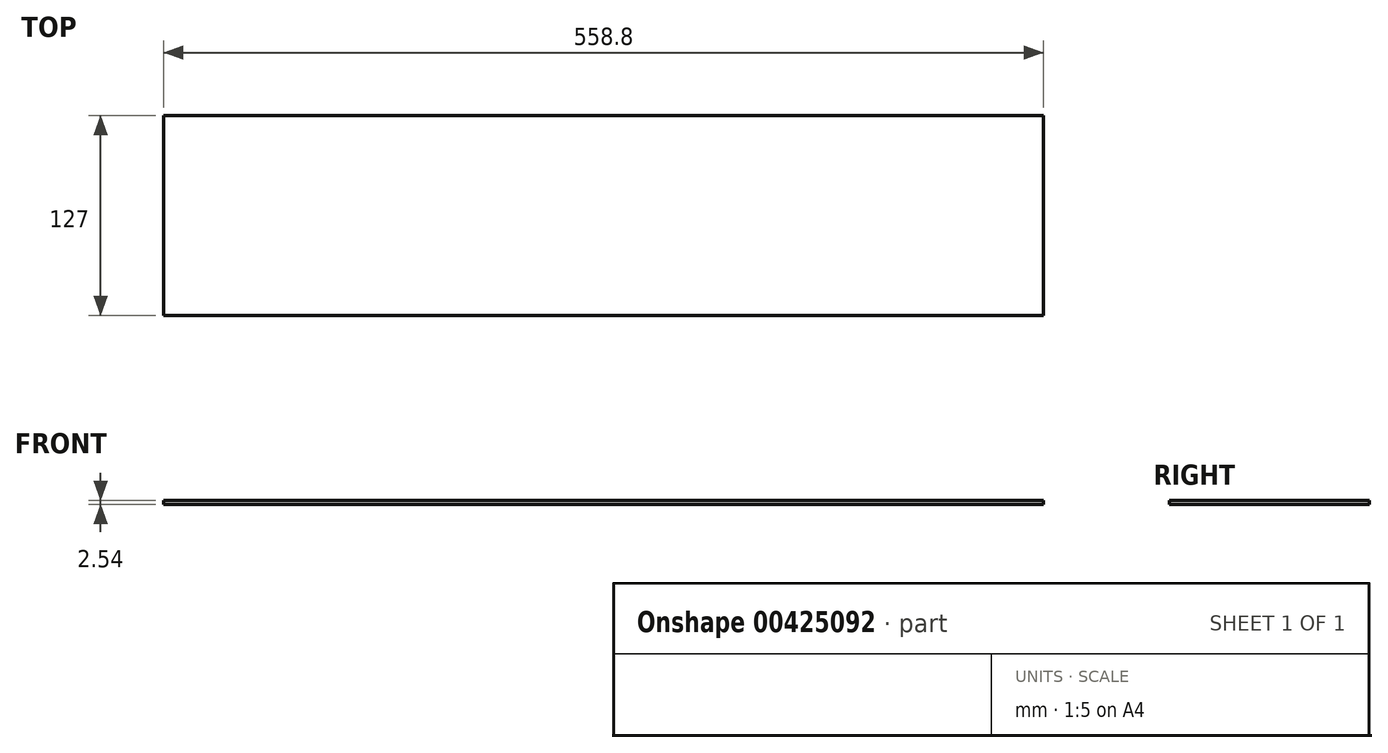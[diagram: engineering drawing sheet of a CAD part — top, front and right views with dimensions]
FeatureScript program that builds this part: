
annotation { "Feature Type Name" : "Feature", "Feature Type Description" : "" }
export const myFeature = defineFeature(function(context is Context, id is Id, definition is map)
    precondition{}
    {
        {
            var Q0;
            Q0=qCreatedBy(makeId("Front.planeOp"),FACE);
            var sketch = newSketch(context, id + "F0", { "sketchPlane" : qUnion([Q0])});
            skLineSegment(sketch, "E0.bottom", {"start": v(-871.4, 83) * mm, "end": v(-312.6, 83) * mm});
            skLineSegment(sketch, "E0.top", {"start": v(-871.4, 80.45) * mm, "end": v(-312.6, 80.45) * mm});
            skLineSegment(sketch, "E0.left", {"start": v(-871.4, 83) * mm, "end": v(-871.4, 80.45) * mm});
            skLineSegment(sketch, "E0.right", {"start": v(-312.6, 83) * mm, "end": v(-312.6, 80.45) * mm});
            skSolve(sketch);
        }
        {
            var Q0;
            Q0=makeQuery(id+"F0.imprint","IMPRINT",FACE,{"disambiguationData":[TD([[makeQuery(id+"F0.imprint","IMPRINT",EDGE,{"derivedFrom":sQuery(id+"F0.wireOp",EDGE,"E0.bottom")}),-1.0]])]});
            extrude(context, id + "F1", {"entities" : qUnion([Q0]), "depth" : 127 * mm});
        }
    });
